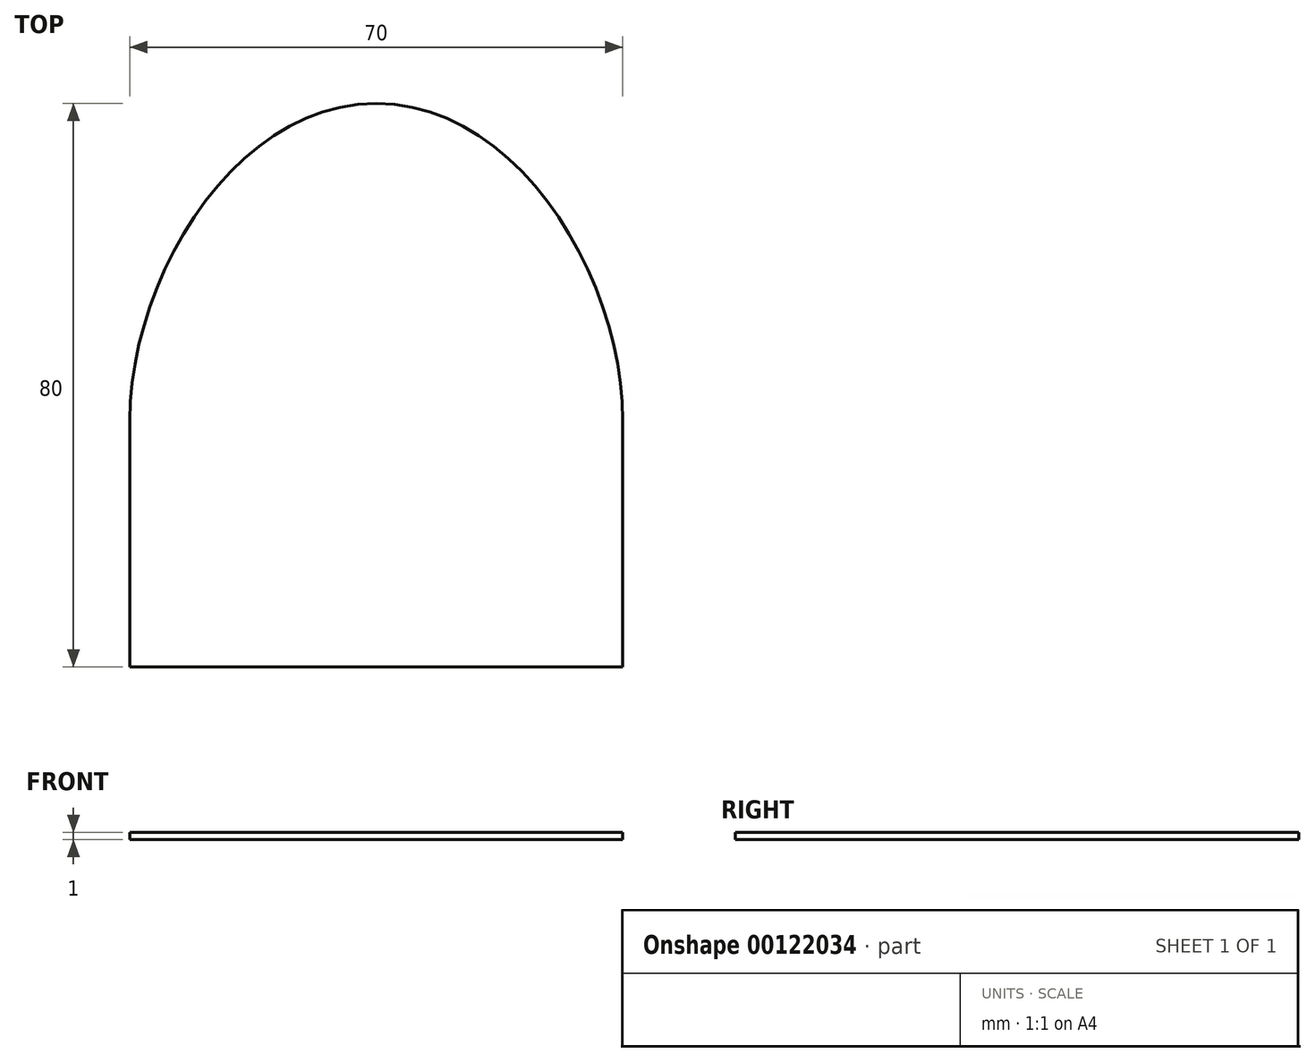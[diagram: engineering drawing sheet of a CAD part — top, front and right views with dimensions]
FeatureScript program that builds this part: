
annotation { "Feature Type Name" : "Feature", "Feature Type Description" : "" }
export const myFeature = defineFeature(function(context is Context, id is Id, definition is map)
    precondition{}
    {
        {
            var Q0;
            Q0=qCreatedBy(makeId("Top.planeOp"),FACE);
            var sketch = newSketch(context, id + "F0", { "sketchPlane" : qUnion([Q0])});
            skLineSegment(sketch, "E0.top", {"start": v(-35, -35) * mm, "end": v(35, -35) * mm});
            skPoint(sketch, "E0.middle", {"position": v(0, 13.14) * mm});
            skPoint(sketch, "E1", {"position": v(0, 0) * mm});
            skCircle(sketch, "E2", {"center": v(0, 0) * mm, "radius": 35 * mm});
            skPoint(sketch, "E3.visualSharp", {"position": v(-35, -35) * mm});
            skPoint(sketch, "E4.visualSharp", {"position": v(35, -35) * mm});
            skPoint(sketch, "E5", {"position": v(-35, 0) * mm});
            skPoint(sketch, "E6", {"position": v(35, 0) * mm});
            skFitSpline(sketch, "E7", {"points": [v(0, 45) * mm, v(-35, 0) * mm], "startDerivative": vector(-60.6, 0) * mm, "endDerivative": vector(0, -60.15) * mm});
            skLineSegment(sketch, "E8", {"start": v(-35, 0) * mm, "end": v(-35, -35) * mm});
            skLineSegment(sketch, "E9", {"start": v(35, 0) * mm, "end": v(35, -35) * mm});
            skFitSpline(sketch, "E10.MirrorCS", {"points": [v(0, 45) * mm, v(35, 0) * mm], "startDerivative": vector(60.6, 0) * mm, "endDerivative": vector(0, -60.15) * mm});
            skFitSpline(sketch, "E11.0", {"points": [v(0, 37) * mm, v(-0.85, 37) * mm, v(-2.51, 36.87) * mm, v(-4.95, 36.3) * mm, v(-7.36, 35.37) * mm, v(-10.54, 33.64) * mm, v(-14.42, 30.55) * mm, v(-18.67, 25.54) * mm, v(-22.24, 19.56) * mm, v(-24.95, 13) * mm, v(-26.62, 6.3) * mm, v(-27, 2.01) * mm, v(-27, 0) * mm]});
            skPoint(sketch, "E12", {"position": v(0, 37) * mm});
            skPoint(sketch, "E13", {"position": v(-7.77, 35.11) * mm});
            skPoint(sketch, "E14", {"position": v(-14.26, 30.43) * mm});
            skPoint(sketch, "E15", {"position": v(-19.34, 24.24) * mm});
            skPoint(sketch, "E16", {"position": v(-23.15, 17.21) * mm});
            skPoint(sketch, "E17", {"position": v(-25.74, 9.64) * mm});
            skLineSegment(sketch, "E18", {"start": v(-27, 0) * mm, "end": v(-27, -35) * mm});
            skPoint(sketch, "E19", {"position": v(-26.96, 1.74) * mm});
            skPoint(sketch, "E20", {"position": v(-25.02, 3.05) * mm});
            skSolve(sketch);
        }
        {
            var Q0;
            Q0=qSketchRegion(id+"F0",true);
            extrude(context, id + "F1", {"entities" : qUnion([Q0]), "depth" : 1 * mm});
        }
    });
